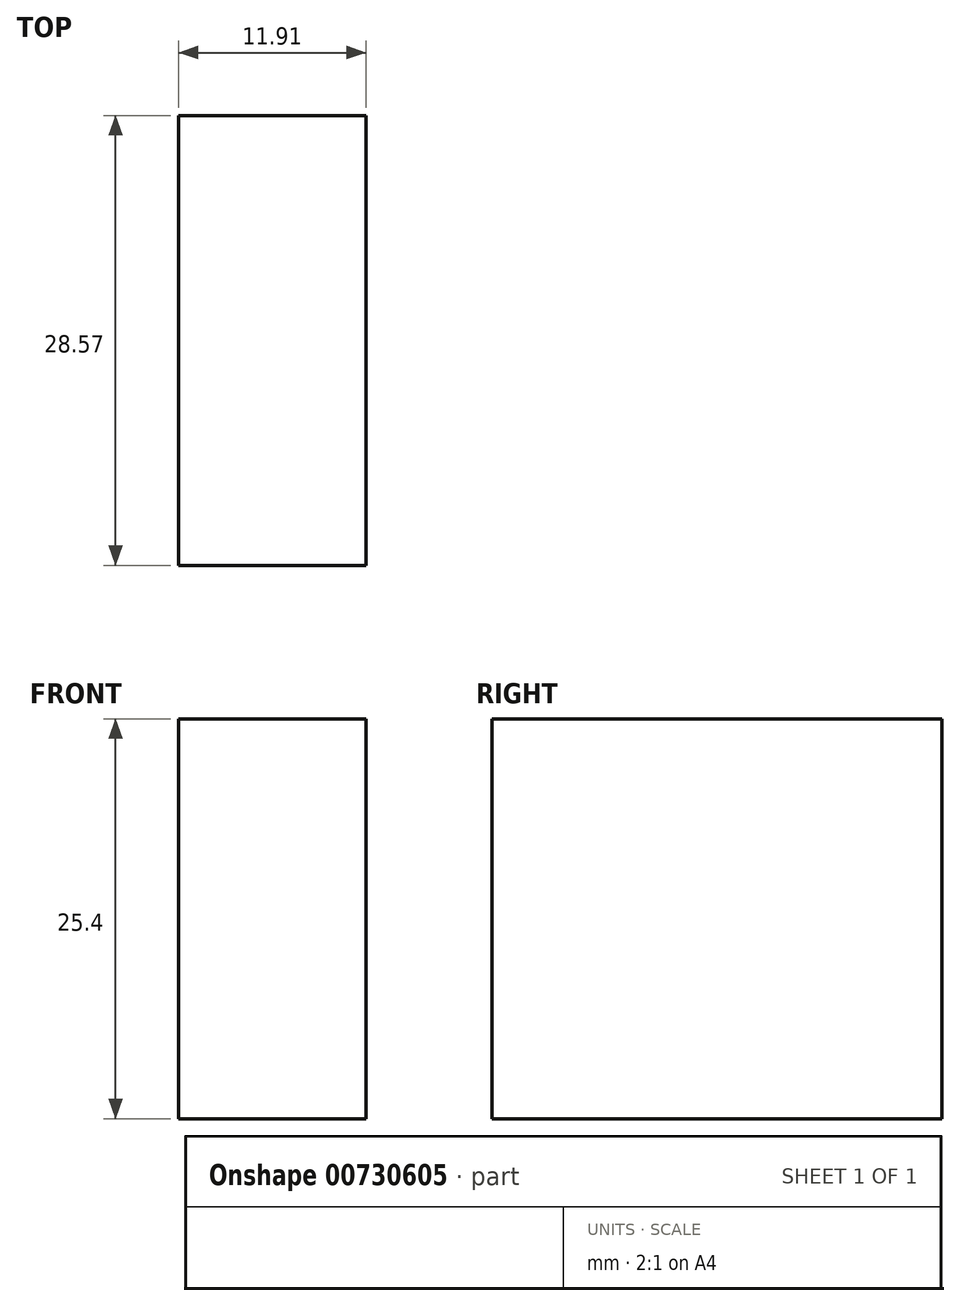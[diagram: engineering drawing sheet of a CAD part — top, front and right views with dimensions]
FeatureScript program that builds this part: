
annotation { "Feature Type Name" : "Feature", "Feature Type Description" : "" }
export const myFeature = defineFeature(function(context is Context, id is Id, definition is map)
    precondition{}
    {
        {
            var Q0;
            Q0=qCreatedBy(makeId("Top.planeOp"),FACE);
            var sketch = newSketch(context, id + "F0", { "sketchPlane" : qUnion([Q0])});
            skLineSegment(sketch, "E0.bottom", {"start": v(0, 0) * mm, "end": v(11.9, 0) * mm});
            skLineSegment(sketch, "E0.top", {"start": v(0, 28.58) * mm, "end": v(11.9, 28.58) * mm});
            skLineSegment(sketch, "E0.left", {"start": v(0, 0) * mm, "end": v(0, 28.58) * mm});
            skLineSegment(sketch, "E0.right", {"start": v(11.9, 0) * mm, "end": v(11.9, 28.58) * mm});
            skSolve(sketch);
        }
        {
            var Q0;
            Q0=makeQuery(id+"F0.imprint","IMPRINT",FACE,{"disambiguationData":[TD([[makeQuery(id+"F0.imprint","IMPRINT",EDGE,{"derivedFrom":sQuery(id+"F0.wireOp",EDGE,"E0.bottom")}),1.0]])]});
            extrude(context, id + "F1", {"entities" : qUnion([Q0]), "depth" : 25.4 * mm, "offsetDistance" : 25.4 * mm});
        }
    });
